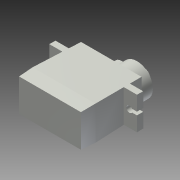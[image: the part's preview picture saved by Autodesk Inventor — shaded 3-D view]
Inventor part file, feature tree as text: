
AUTODESK INVENTOR PART (.ipt)
format: ipt  version: 2015 (Build 190159000, 159)  size: 216,576 bytes
history: native  units: mm
features: sketch x7, plane x6, extrude x4, loft x2, mirror x1, split x1, other x1
ambient origin geometry x8: Origin, YZ Plane, XZ Plane, XY Plane, X Axis, Y Axis, Z Axis, Center Point
bodies: Solid2 (feature_tree), Solid3 (feature_tree), Solid4 (feature_tree)
feature tree (22):
  sketch  "Sketch1"  dims[d0=22.8mm d1=12.0mm]
  plane  "Work Plane3"
  loft  "Loft1"
  plane  "Work Plane4"
  loft  "Loft2"
  plane  "Work Plane5"
  plane  "Work Plane7"
  plane  "Work Plane8"
  extrude  "Extrusion6"  TaperAngle=0.0deg  [1 undecoded]
  extrude  "Extrusion5"  TaperAngle=0.0deg  [1 undecoded]
  mirror  "Mirror3"
  extrude  "Extrusion7"  Depth=4.8mm
  extrude  "Extrusion8"  Depth=1.0mm
  plane  "Work Plane9"
  split  "Split1"
  sketch  "Sketch5"  dims[d32=23.2mm d33=12.5mm]
  sketch  "Sketch7"  dims[d34=0.0mm d35=90.0deg d36=0.0mm d37=90.0deg]
  other  "Edges1"
  sketch  "Sketch9"  dims[d38=22.6mm d50=0.0mm d51=90.0deg]
  sketch  "Sketch10"  dims[d52=0.0mm d53=90.0deg d58=4.8mm]
  sketch  "Sketch11"  dims[d59=4.8mm d60=1.0mm]
  sketch  "Sketch12"  dims[d62=1.2mm d63=4.5mm d64=0.0mm d65=-11.4mm d66=4.9mm d67=0.0mm d68=0.0mm d69=0.0mm d70=0.0mm d71=3.0mm d72=2.8mm d73=14.6mm d74=5.9mm d75=4.2mm d76=0.0mm d77=4.6mm d78=1.5mm d79=2.7mm d80=0.0mm d81=0.0mm d9=1.0mm d10=1.0mm]
note: 2 required parameter values undecoded (feature->parameter linkage not recoverable at this tier; creation-order binding heuristic only, values carry confidence <= 0.55)
